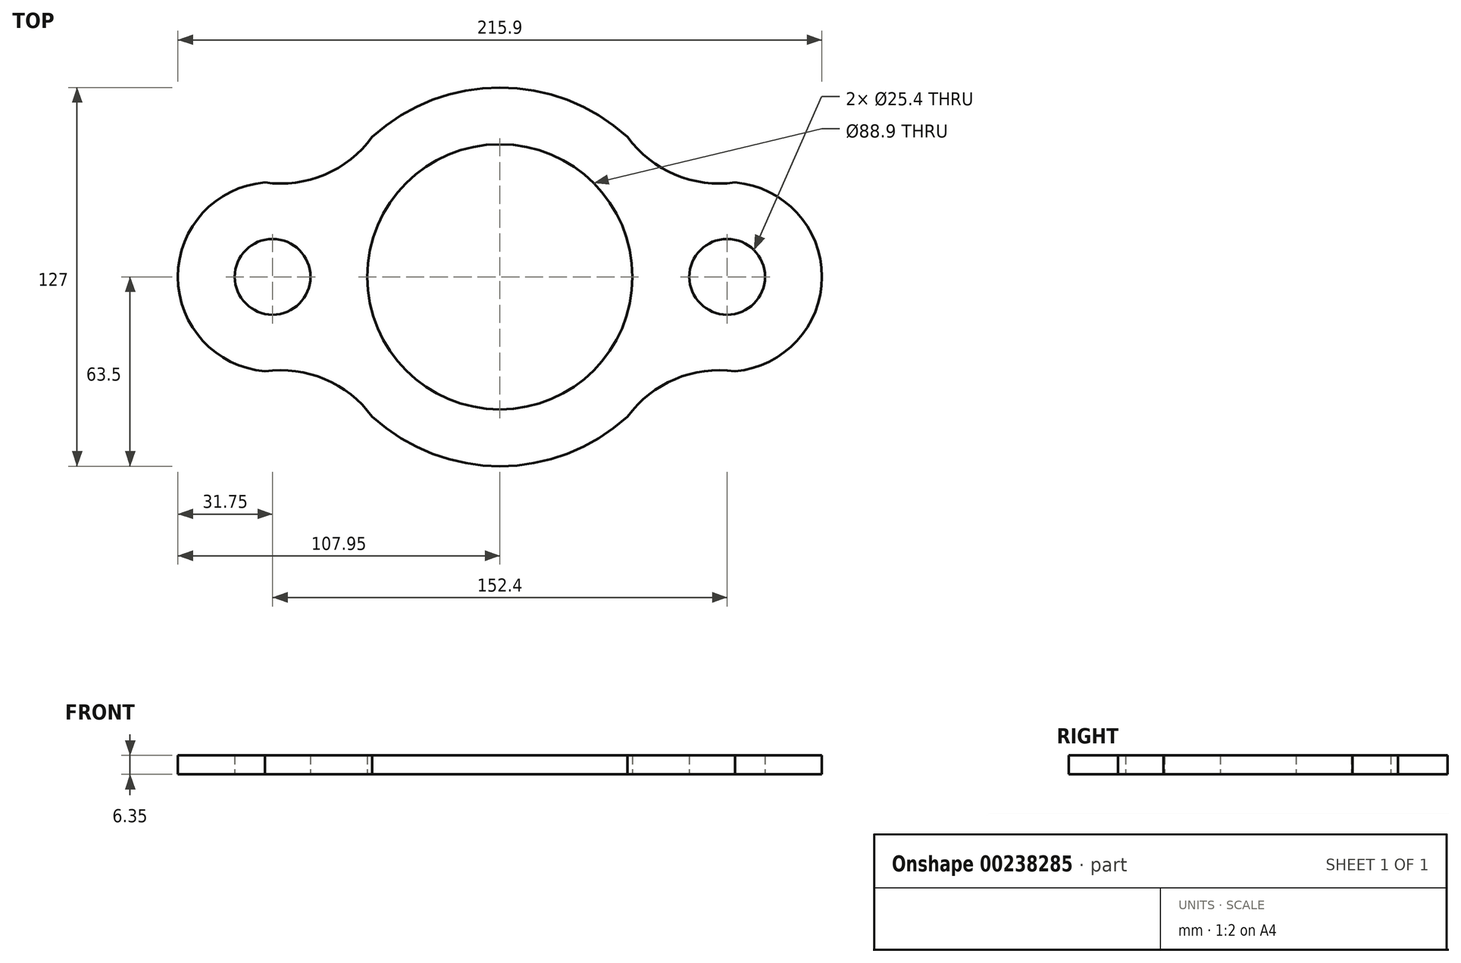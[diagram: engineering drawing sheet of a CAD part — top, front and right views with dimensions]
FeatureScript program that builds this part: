
annotation { "Feature Type Name" : "Feature", "Feature Type Description" : "" }
export const myFeature = defineFeature(function(context is Context, id is Id, definition is map)
    precondition{}
    {
        {
            var Q0;
            Q0=qCreatedBy(makeId("Top.planeOp"),FACE);
            var sketch = newSketch(context, id + "F0", { "sketchPlane" : qUnion([Q0])});
            skCircle(sketch, "E0", {"center": v(0, 0) * mm, "radius": 44.45 * mm});
            skArc(sketch, "E1", {"start": v(-49.32, -40) * mm, "mid": v(0, -63.5) * mm, "end": v(49.32, -40) * mm});
            skArc(sketch, "E2", {"start": v(-71.2, 31.35) * mm, "mid": v(-107.95, 0) * mm, "end": v(-71.2, -31.35) * mm});
            skCircle(sketch, "E3", {"center": v(-76.2, 0) * mm, "radius": 12.7 * mm});
            skCircle(sketch, "E4.MirrorC", {"center": v(76.2, 0) * mm, "radius": 12.7 * mm});
            skArc(sketch, "E5.MirrorCS", {"start": v(71.2, 31.35) * mm, "mid": v(107.95, 0) * mm, "end": v(71.2, -31.35) * mm});
            skArc(sketch, "E6.trimOffspring", {"start": v(49.32, 40) * mm, "mid": v(0, 63.5) * mm, "end": v(-49.32, 40) * mm});
            skArc(sketch, "E7", {"start": v(-78.82, 31.64) * mm, "mid": v(-58.72, 34.3) * mm, "end": v(-42.82, 46.89) * mm});
            skArc(sketch, "E8.MirrorCS", {"start": v(-78.82, -31.64) * mm, "mid": v(-58.72, -34.3) * mm, "end": v(-42.82, -46.89) * mm});
            skArc(sketch, "E9.MirrorCS", {"start": v(78.82, 31.64) * mm, "mid": v(58.72, 34.3) * mm, "end": v(42.82, 46.89) * mm});
            skArc(sketch, "E10.MirrorCS", {"start": v(78.82, -31.64) * mm, "mid": v(58.72, -34.3) * mm, "end": v(42.82, -46.89) * mm});
            skSolve(sketch);
        }
        {
            var Q0;
            Q0=makeQuery(id+"F0.imprint","IMPRINT",FACE,{"disambiguationData":[TD([[makeQuery(id+"F0.imprint","IMPRINT",EDGE,{"derivedFrom":sQuery(id+"F0.wireOp",EDGE,"E0")}),-1.0]])]});
            extrude(context, id + "F1", {"entities" : qUnion([Q0]), "depth" : 6.35 * mm});
        }
    });
